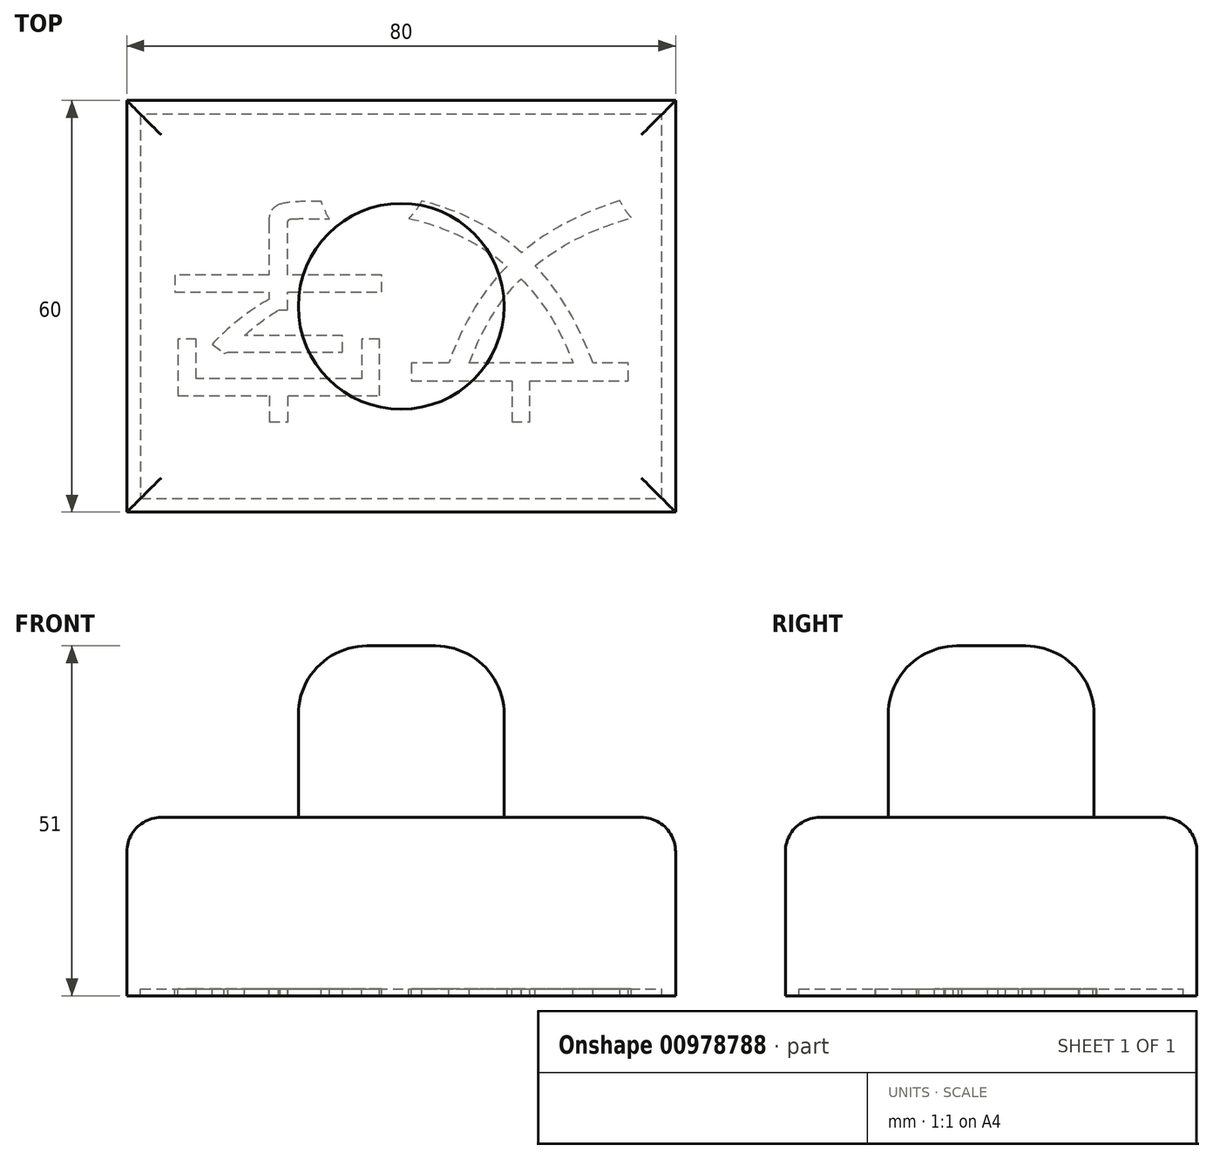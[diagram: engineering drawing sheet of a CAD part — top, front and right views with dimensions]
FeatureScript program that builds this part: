
annotation { "Feature Type Name" : "Feature", "Feature Type Description" : "" }
export const myFeature = defineFeature(function(context is Context, id is Id, definition is map)
    precondition{}
    {
        {
            var Q0;
            Q0=qCreatedBy(makeId("Top.planeOp"),FACE);
            var sketch = newSketch(context, id + "F0", { "sketchPlane" : qUnion([Q0])});
            skLineSegment(sketch, "E0.bottom", {"start": v(40, 30) * mm, "end": v(-40, 30) * mm});
            skLineSegment(sketch, "E0.top", {"start": v(40, -30) * mm, "end": v(-40, -30) * mm});
            skLineSegment(sketch, "E0.left", {"start": v(40, 30) * mm, "end": v(40, -30) * mm});
            skLineSegment(sketch, "E0.right", {"start": v(-40, 30) * mm, "end": v(-40, -30) * mm});
            skPoint(sketch, "E0.middle", {"position": v(0, 0) * mm});
            skSolve(sketch);
        }
        {
            var Q0;
            Q0 = qSketchRegion(id + "F0", true);
            extrude(context, id + "F1", {"entities" : qUnion([Q0]), "depth" : 25 * mm, "offsetDistance" : 25 * mm});
        }
        {
            var Q0;
            Q0=makeQuery(id+"F1.opExtrude","CAP_FACE",FACE,{"disambiguationData":[OSD([sQuery(id+"F0.wireOp",EDGE,"E0.bottom"),sQuery(id+"F0.wireOp",EDGE,"E0.top"),sQuery(id+"F0.wireOp",EDGE,"E0.left"),sQuery(id+"F0.wireOp",EDGE,"E0.right")])],"isStart":false});
            var sketch = newSketch(context, id + "F2", { "sketchPlane" : qUnion([Q0])});
            skCircle(sketch, "E1", {"center": v(0, 0) * mm, "radius": 15 * mm});
            skSolve(sketch);
        }
        {
            var Q0;
            Q0 = qSketchRegion(id + "F2", true);
            extrude(context, id + "F3", {"entities" : qUnion([Q0]), "operationType" : NewBodyOperationType.ADD, "depth" : 25 * mm, "offsetDistance" : 25 * mm});
        }
        {
            var Q0;
            Q0=makeQuery(id+"F1.opExtrude","CAP_EDGE",EDGE,{"disambiguationData":[OSD([sQuery(id+"F0.wireOp",EDGE,"E0.left")])],"isStart":false});
            var Q1;
            Q1=makeQuery(id+"F1.opExtrude","CAP_EDGE",EDGE,{"disambiguationData":[OSD([sQuery(id+"F0.wireOp",EDGE,"E0.bottom")])],"isStart":false});
            var Q2;
            Q2=makeQuery(id+"F1.opExtrude","CAP_EDGE",EDGE,{"disambiguationData":[OSD([sQuery(id+"F0.wireOp",EDGE,"E0.right")])],"isStart":false});
            var Q3;
            Q3=makeQuery(id+"F1.opExtrude","CAP_EDGE",EDGE,{"disambiguationData":[OSD([sQuery(id+"F0.wireOp",EDGE,"E0.top")])],"isStart":false});
            var Q4;
            Q4=makeQuery(id+"F3.opExtrude","CAP_EDGE",EDGE,{"disambiguationData":[OSD([sQuery(id+"F2.wireOp",EDGE,"E1")])],"isStart":true});
            fillet(context, id + "F4", {"entities" : qUnion([Q0, Q1, Q2, Q3, Q4]), "radius" : 5 * mm, "tangentPropagation" : true, "allowEdgeOverflow" : false});
        }
        {
            var Q0;
            Q0=makeQuery(id+"F3.opExtrude","CAP_EDGE",EDGE,{"disambiguationData":[OSD([sQuery(id+"F2.wireOp",EDGE,"E1")])],"isStart":false});
            fillet(context, id + "F5", {"entities" : qUnion([Q0]), "radius" : 10 * mm, "tangentPropagation" : true, "allowEdgeOverflow" : false});
        }
        {
            var Q0;
            Q0=makeQuery(id+"F1.opExtrude","CAP_FACE",FACE,{"disambiguationData":[OSD([sQuery(id+"F0.wireOp",EDGE,"E0.bottom"),sQuery(id+"F0.wireOp",EDGE,"E0.top"),sQuery(id+"F0.wireOp",EDGE,"E0.left"),sQuery(id+"F0.wireOp",EDGE,"E0.right")])],"isStart":true});
            var sketch = newSketch(context, id + "F6", { "sketchPlane" : qUnion([Q0])});
            skText(sketch, "E2", { "text": "文字", "fontName": "NotoSansCJKjp-Regular.otf"});
            const initialGuessF6  = {"E2": [-0.035, -0.0127, 1, 0, 0.0254]};
            skSetInitialGuess(sketch, initialGuessF6);
            skSolve(sketch);
        }
        {
            var Q0;
            Q0 = qSketchRegion(id + "F6", true);
            extrude(context, id + "F7", {"entities" : qUnion([Q0]), "oppositeDirection" : true, "depth" : 1 * mm, "offsetDistance" : 25 * mm});
        }
        {
            var Q0;
            Q0=makeQuery(id+"F7.opExtrude","SWEPT_BODY",BODY,{"disambiguationData":[OSD([sQuery(id+"F6.wireOp",EDGE,"E2.sketch_text.stroke-32"),sQuery(id+"F6.wireOp",EDGE,"E2.sketch_text.stroke-33"),sQuery(id+"F6.wireOp",EDGE,"E2.sketch_text.stroke-34"),sQuery(id+"F6.wireOp",EDGE,"E2.sketch_text.stroke-35"),sQuery(id+"F6.wireOp",EDGE,"E2.sketch_text.stroke-36"),sQuery(id+"F6.wireOp",EDGE,"E2.sketch_text.stroke-37"),sQuery(id+"F6.wireOp",EDGE,"E2.sketch_text.stroke-38"),sQuery(id+"F6.wireOp",EDGE,"E2.sketch_text.stroke-39"),sQuery(id+"F6.wireOp",EDGE,"E2.sketch_text.stroke-40"),sQuery(id+"F6.wireOp",EDGE,"E2.sketch_text.stroke-41"),sQuery(id+"F6.wireOp",EDGE,"E2.sketch_text.stroke-42"),sQuery(id+"F6.wireOp",EDGE,"E2.sketch_text.stroke-43"),sQuery(id+"F6.wireOp",EDGE,"E2.sketch_text.stroke-44"),sQuery(id+"F6.wireOp",EDGE,"E2.sketch_text.stroke-45"),sQuery(id+"F6.wireOp",EDGE,"E2.sketch_text.stroke-46"),sQuery(id+"F6.wireOp",EDGE,"E2.sketch_text.stroke-47"),sQuery(id+"F6.wireOp",EDGE,"E2.sketch_text.stroke-48"),sQuery(id+"F6.wireOp",EDGE,"E2.sketch_text.stroke-49"),sQuery(id+"F6.wireOp",EDGE,"E2.sketch_text.stroke-50"),sQuery(id+"F6.wireOp",EDGE,"E2.sketch_text.stroke-51"),sQuery(id+"F6.wireOp",EDGE,"E2.sketch_text.stroke-52"),sQuery(id+"F6.wireOp",EDGE,"E2.sketch_text.stroke-53"),sQuery(id+"F6.wireOp",EDGE,"E2.sketch_text.stroke-54")])]});
            var Q1;
            Q1=makeQuery(id+"F7.opExtrude","SWEPT_BODY",BODY,{"disambiguationData":[OSD([sQuery(id+"F6.wireOp",EDGE,"E2.sketch_text.stroke-20"),sQuery(id+"F6.wireOp",EDGE,"E2.sketch_text.stroke-21"),sQuery(id+"F6.wireOp",EDGE,"E2.sketch_text.stroke-22"),sQuery(id+"F6.wireOp",EDGE,"E2.sketch_text.stroke-23"),sQuery(id+"F6.wireOp",EDGE,"E2.sketch_text.stroke-24"),sQuery(id+"F6.wireOp",EDGE,"E2.sketch_text.stroke-25"),sQuery(id+"F6.wireOp",EDGE,"E2.sketch_text.stroke-26"),sQuery(id+"F6.wireOp",EDGE,"E2.sketch_text.stroke-27"),sQuery(id+"F6.wireOp",EDGE,"E2.sketch_text.stroke-28"),sQuery(id+"F6.wireOp",EDGE,"E2.sketch_text.stroke-29"),sQuery(id+"F6.wireOp",EDGE,"E2.sketch_text.stroke-30"),sQuery(id+"F6.wireOp",EDGE,"E2.sketch_text.stroke-31")])]});
            var Q2;
            Q2=makeQuery(id+"F7.opExtrude","SWEPT_BODY",BODY,{"disambiguationData":[OSD([sQuery(id+"F6.wireOp",EDGE,"E2.sketch_text.stroke-0"),sQuery(id+"F6.wireOp",EDGE,"E2.sketch_text.stroke-1"),sQuery(id+"F6.wireOp",EDGE,"E2.sketch_text.stroke-2"),sQuery(id+"F6.wireOp",EDGE,"E2.sketch_text.stroke-3"),sQuery(id+"F6.wireOp",EDGE,"E2.sketch_text.stroke-4"),sQuery(id+"F6.wireOp",EDGE,"E2.sketch_text.stroke-5"),sQuery(id+"F6.wireOp",EDGE,"E2.sketch_text.stroke-6"),sQuery(id+"F6.wireOp",EDGE,"E2.sketch_text.stroke-7"),sQuery(id+"F6.wireOp",EDGE,"E2.sketch_text.stroke-8"),sQuery(id+"F6.wireOp",EDGE,"E2.sketch_text.stroke-9"),sQuery(id+"F6.wireOp",EDGE,"E2.sketch_text.stroke-10"),sQuery(id+"F6.wireOp",EDGE,"E2.sketch_text.stroke-11"),sQuery(id+"F6.wireOp",EDGE,"E2.sketch_text.stroke-12"),sQuery(id+"F6.wireOp",EDGE,"E2.sketch_text.stroke-13"),sQuery(id+"F6.wireOp",EDGE,"E2.sketch_text.stroke-14"),sQuery(id+"F6.wireOp",EDGE,"E2.sketch_text.stroke-15"),sQuery(id+"F6.wireOp",EDGE,"E2.sketch_text.stroke-16"),sQuery(id+"F6.wireOp",EDGE,"E2.sketch_text.stroke-17"),sQuery(id+"F6.wireOp",EDGE,"E2.sketch_text.stroke-18"),sQuery(id+"F6.wireOp",EDGE,"E2.sketch_text.stroke-19")])]});
            var Q3;
            Q3=sQuery(id+"F6.wireOp",EDGE,"E2.sketch_text.center");
            transform(context, id + "F8", {"entities" : qUnion([Q0, Q1, Q2]), "transformType" : TransformType.ROTATION, "transformAxis" : qUnion([Q3]), "angle" : 180 * degree, "makeCopy" : false});
        }
        {
            var Q0;
            Q0=makeQuery(id+"F1.opExtrude","SWEPT_BODY",BODY,{"disambiguationData":[OSD([sQuery(id+"F0.wireOp",EDGE,"E0.bottom"),sQuery(id+"F0.wireOp",EDGE,"E0.top"),sQuery(id+"F0.wireOp",EDGE,"E0.left"),sQuery(id+"F0.wireOp",EDGE,"E0.right")])]});
            var Q1;
            Q1=makeQuery(id+"F7.opExtrude","SWEPT_BODY",BODY,{"disambiguationData":[OSD([sQuery(id+"F6.wireOp",EDGE,"E2.sketch_text.stroke-20"),sQuery(id+"F6.wireOp",EDGE,"E2.sketch_text.stroke-21"),sQuery(id+"F6.wireOp",EDGE,"E2.sketch_text.stroke-22"),sQuery(id+"F6.wireOp",EDGE,"E2.sketch_text.stroke-23"),sQuery(id+"F6.wireOp",EDGE,"E2.sketch_text.stroke-24"),sQuery(id+"F6.wireOp",EDGE,"E2.sketch_text.stroke-25"),sQuery(id+"F6.wireOp",EDGE,"E2.sketch_text.stroke-26"),sQuery(id+"F6.wireOp",EDGE,"E2.sketch_text.stroke-27"),sQuery(id+"F6.wireOp",EDGE,"E2.sketch_text.stroke-28"),sQuery(id+"F6.wireOp",EDGE,"E2.sketch_text.stroke-29"),sQuery(id+"F6.wireOp",EDGE,"E2.sketch_text.stroke-30"),sQuery(id+"F6.wireOp",EDGE,"E2.sketch_text.stroke-31")])]});
            var Q2;
            Q2=makeQuery(id+"F7.opExtrude","SWEPT_BODY",BODY,{"disambiguationData":[OSD([sQuery(id+"F6.wireOp",EDGE,"E2.sketch_text.stroke-32"),sQuery(id+"F6.wireOp",EDGE,"E2.sketch_text.stroke-33"),sQuery(id+"F6.wireOp",EDGE,"E2.sketch_text.stroke-34"),sQuery(id+"F6.wireOp",EDGE,"E2.sketch_text.stroke-35"),sQuery(id+"F6.wireOp",EDGE,"E2.sketch_text.stroke-36"),sQuery(id+"F6.wireOp",EDGE,"E2.sketch_text.stroke-37"),sQuery(id+"F6.wireOp",EDGE,"E2.sketch_text.stroke-38"),sQuery(id+"F6.wireOp",EDGE,"E2.sketch_text.stroke-39"),sQuery(id+"F6.wireOp",EDGE,"E2.sketch_text.stroke-40"),sQuery(id+"F6.wireOp",EDGE,"E2.sketch_text.stroke-41"),sQuery(id+"F6.wireOp",EDGE,"E2.sketch_text.stroke-42"),sQuery(id+"F6.wireOp",EDGE,"E2.sketch_text.stroke-43"),sQuery(id+"F6.wireOp",EDGE,"E2.sketch_text.stroke-44"),sQuery(id+"F6.wireOp",EDGE,"E2.sketch_text.stroke-45"),sQuery(id+"F6.wireOp",EDGE,"E2.sketch_text.stroke-46"),sQuery(id+"F6.wireOp",EDGE,"E2.sketch_text.stroke-47"),sQuery(id+"F6.wireOp",EDGE,"E2.sketch_text.stroke-48"),sQuery(id+"F6.wireOp",EDGE,"E2.sketch_text.stroke-49"),sQuery(id+"F6.wireOp",EDGE,"E2.sketch_text.stroke-50"),sQuery(id+"F6.wireOp",EDGE,"E2.sketch_text.stroke-51"),sQuery(id+"F6.wireOp",EDGE,"E2.sketch_text.stroke-52"),sQuery(id+"F6.wireOp",EDGE,"E2.sketch_text.stroke-53"),sQuery(id+"F6.wireOp",EDGE,"E2.sketch_text.stroke-54")])]});
            var Q3;
            Q3=makeQuery(id+"F7.opExtrude","SWEPT_BODY",BODY,{"disambiguationData":[OSD([sQuery(id+"F6.wireOp",EDGE,"E2.sketch_text.stroke-0"),sQuery(id+"F6.wireOp",EDGE,"E2.sketch_text.stroke-1"),sQuery(id+"F6.wireOp",EDGE,"E2.sketch_text.stroke-2"),sQuery(id+"F6.wireOp",EDGE,"E2.sketch_text.stroke-3"),sQuery(id+"F6.wireOp",EDGE,"E2.sketch_text.stroke-4"),sQuery(id+"F6.wireOp",EDGE,"E2.sketch_text.stroke-5"),sQuery(id+"F6.wireOp",EDGE,"E2.sketch_text.stroke-6"),sQuery(id+"F6.wireOp",EDGE,"E2.sketch_text.stroke-7"),sQuery(id+"F6.wireOp",EDGE,"E2.sketch_text.stroke-8"),sQuery(id+"F6.wireOp",EDGE,"E2.sketch_text.stroke-9"),sQuery(id+"F6.wireOp",EDGE,"E2.sketch_text.stroke-10"),sQuery(id+"F6.wireOp",EDGE,"E2.sketch_text.stroke-11"),sQuery(id+"F6.wireOp",EDGE,"E2.sketch_text.stroke-12"),sQuery(id+"F6.wireOp",EDGE,"E2.sketch_text.stroke-13"),sQuery(id+"F6.wireOp",EDGE,"E2.sketch_text.stroke-14"),sQuery(id+"F6.wireOp",EDGE,"E2.sketch_text.stroke-15"),sQuery(id+"F6.wireOp",EDGE,"E2.sketch_text.stroke-16"),sQuery(id+"F6.wireOp",EDGE,"E2.sketch_text.stroke-17"),sQuery(id+"F6.wireOp",EDGE,"E2.sketch_text.stroke-18"),sQuery(id+"F6.wireOp",EDGE,"E2.sketch_text.stroke-19")])]});
            booleanBodies(context, id + "F9", {"operationType" : BooleanOperationType.UNION, "tools" : qUnion([Q0, Q1, Q2, Q3])});
        }
        {
            var Q0;
            {var subQ0=sQuery(id+"F0.wireOp",EDGE,"E0.right");var subQ1=sQuery(id+"F0.wireOp",EDGE,"E0.left");var subQ2=sQuery(id+"F0.wireOp",EDGE,"E0.top");var subQ3=sQuery(id+"F0.wireOp",EDGE,"E0.bottom");Q0=makeQuery(id+"F9.opBoolean","SPLIT",FACE,{"disambiguationData":[TD([makeQuery(id+"F1.opExtrude","SWEPT_FACE",FACE,{"disambiguationData":[OSD([subQ3])]})])],"derivedFrom":makeQuery(id+"F1.opExtrude","CAP_FACE",FACE,{"disambiguationData":[OSD([subQ3,subQ2,subQ1,subQ0])],"isStart":true})});}
            var sketch = newSketch(context, id + "F10", { "sketchPlane" : qUnion([Q0])});
            skLineSegment(sketch, "E3.0", {"start": v(38, 28) * mm, "end": v(-38, 28) * mm});
            skLineSegment(sketch, "E3.1", {"start": v(38, -28) * mm, "end": v(38, 28) * mm});
            skLineSegment(sketch, "E3.2", {"start": v(-38, -28) * mm, "end": v(38, -28) * mm});
            skLineSegment(sketch, "E3.3", {"start": v(-38, 28) * mm, "end": v(-38, -28) * mm});
            skLineSegment(sketch, "E4.0", {"start": v(40, 30) * mm, "end": v(-40, 30) * mm});
            skLineSegment(sketch, "E5.0", {"start": v(40, -30) * mm, "end": v(40, 30) * mm});
            skLineSegment(sketch, "E6.0", {"start": v(40, -30) * mm, "end": v(-40, -30) * mm});
            skLineSegment(sketch, "E7.0", {"start": v(-40, -30) * mm, "end": v(-40, 30) * mm});
            skSolve(sketch);
        }
        {
            var Q0;
            Q0 = qSketchRegion(id + "F10", true);
            var Q1;
            Q1=makeQuery(id+"F7.opExtrude","CAP_FACE",FACE,{"disambiguationData":[OSD([sQuery(id+"F6.wireOp",EDGE,"E2.sketch_text.stroke-20"),sQuery(id+"F6.wireOp",EDGE,"E2.sketch_text.stroke-21"),sQuery(id+"F6.wireOp",EDGE,"E2.sketch_text.stroke-22"),sQuery(id+"F6.wireOp",EDGE,"E2.sketch_text.stroke-23"),sQuery(id+"F6.wireOp",EDGE,"E2.sketch_text.stroke-24"),sQuery(id+"F6.wireOp",EDGE,"E2.sketch_text.stroke-25"),sQuery(id+"F6.wireOp",EDGE,"E2.sketch_text.stroke-26"),sQuery(id+"F6.wireOp",EDGE,"E2.sketch_text.stroke-27"),sQuery(id+"F6.wireOp",EDGE,"E2.sketch_text.stroke-28"),sQuery(id+"F6.wireOp",EDGE,"E2.sketch_text.stroke-29"),sQuery(id+"F6.wireOp",EDGE,"E2.sketch_text.stroke-30"),sQuery(id+"F6.wireOp",EDGE,"E2.sketch_text.stroke-31")])],"isStart":false});
            extrude(context, id + "F11", {"entities" : qUnion([Q0]), "operationType" : NewBodyOperationType.ADD, "endBound" : BoundingType.UP_TO_SURFACE, "depth" : 25 * mm, "endBoundEntityFace" : qUnion([Q1]), "offsetDistance" : 25 * mm});
        }
    });
